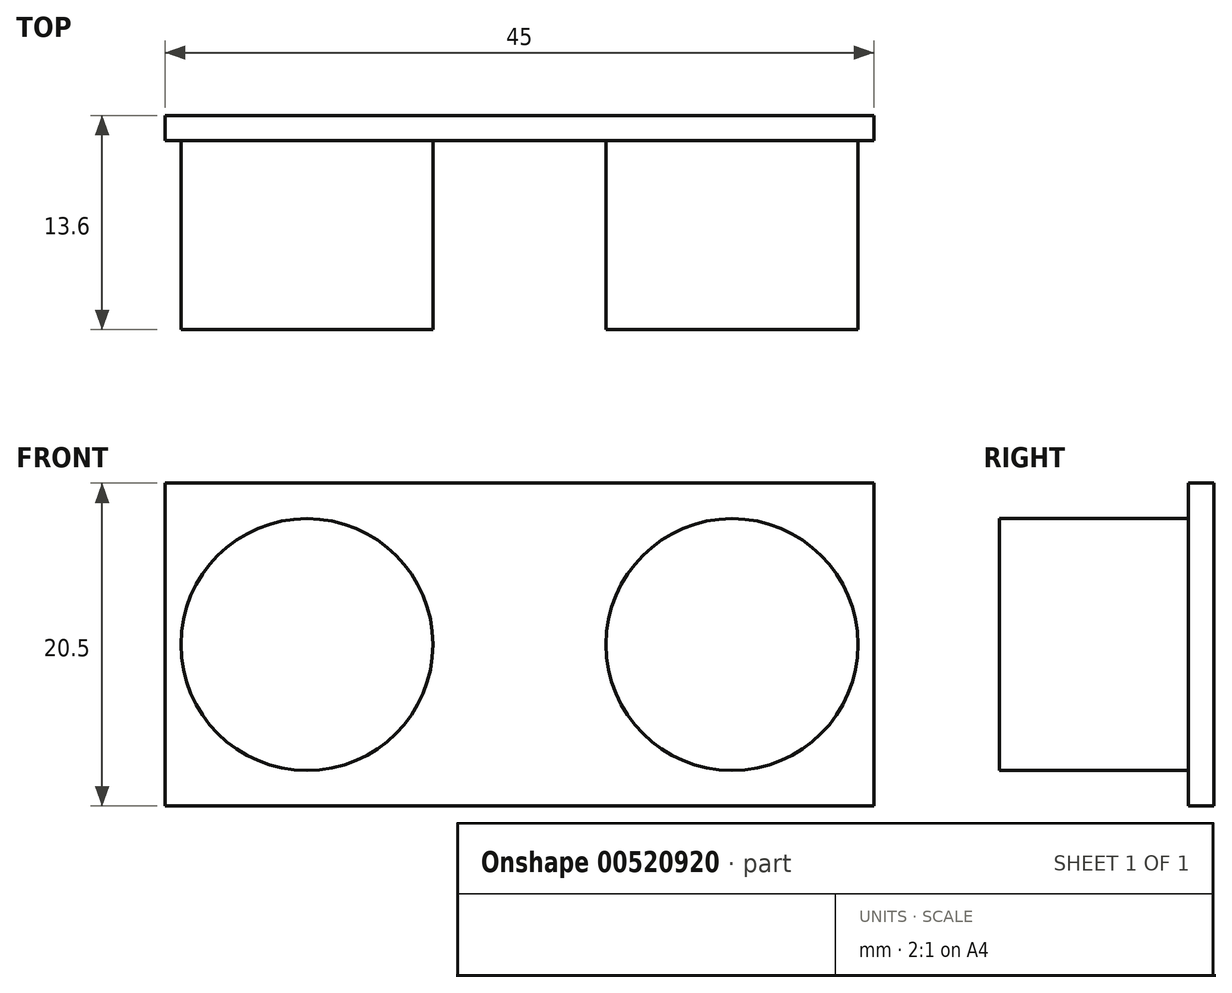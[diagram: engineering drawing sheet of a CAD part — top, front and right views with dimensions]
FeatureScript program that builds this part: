
annotation { "Feature Type Name" : "Feature", "Feature Type Description" : "" }
export const myFeature = defineFeature(function(context is Context, id is Id, definition is map)
    precondition{}
    {
        {
            var Q0;
            Q0=qCreatedBy(makeId("Front.planeOp"),FACE);
            var sketch = newSketch(context, id + "F0", { "sketchPlane" : qUnion([Q0])});
            skLineSegment(sketch, "E0.bottom", {"start": v(-22.5, -10.25) * mm, "end": v(22.5, -10.25) * mm});
            skLineSegment(sketch, "E0.top", {"start": v(-22.5, 10.25) * mm, "end": v(22.5, 10.25) * mm});
            skLineSegment(sketch, "E0.left", {"start": v(-22.5, -10.25) * mm, "end": v(-22.5, 10.25) * mm});
            skLineSegment(sketch, "E0.right", {"start": v(22.5, -10.25) * mm, "end": v(22.5, 10.25) * mm});
            skPoint(sketch, "E0.middle", {"position": v(0, 0) * mm});
            skSolve(sketch);
        }
        {
            var Q0;
            Q0 = qSketchRegion(id + "F0", true);
            extrude(context, id + "F1", {"entities" : qUnion([Q0]), "depth" : 1.6 * mm, "offsetDistance" : 25.4 * mm});
        }
        {
            var Q0;
            Q0=makeQuery(id+"F1.opExtrude","CAP_FACE",FACE,{"disambiguationData":[OSD([sQuery(id+"F0.wireOp",EDGE,"E0.bottom"),sQuery(id+"F0.wireOp",EDGE,"E0.top"),sQuery(id+"F0.wireOp",EDGE,"E0.left"),sQuery(id+"F0.wireOp",EDGE,"E0.right")])],"isStart":false});
            var sketch = newSketch(context, id + "F2", { "sketchPlane" : qUnion([Q0])});
            skCircle(sketch, "E1", {"center": v(-13.5, 0) * mm, "radius": 8 * mm});
            skCircle(sketch, "E2", {"center": v(13.5, 0) * mm, "radius": 8 * mm});
            skLineSegment(sketch, "E3", {"start": v(-5.5, 0) * mm, "end": v(5.5, 0) * mm});
            skLineSegment(sketch, "E4", {"start": v(0, 10.25) * mm, "end": v(0, -10.25) * mm});
            skPoint(sketch, "E5", {"position": v(0, 0) * mm});
            skSolve(sketch);
        }
        {
            var Q0;
            Q0 = qSketchRegion(id + "F2", true);
            extrude(context, id + "F3", {"entities" : qUnion([Q0]), "operationType" : NewBodyOperationType.ADD, "depth" : 12 * mm, "offsetDistance" : 25.4 * mm});
        }
    });
